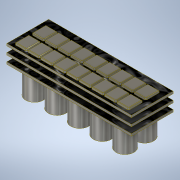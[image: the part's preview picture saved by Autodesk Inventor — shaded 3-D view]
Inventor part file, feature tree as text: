
AUTODESK INVENTOR PART (.ipt)
format: ipt  version: 2020 (Build 240168000, 168)  size: 654,336 bytes
history: native  units: mm
features: chamfer x16, extrude x9, sketch x9, other x2
ambient origin geometry x8: Origin, YZ Plane, XZ Plane, XY Plane, X Axis, Y Axis, Z Axis, Center Point
bodies: Body1 (feature_tree)
feature tree (36):
  other  "Bryła1"
  extrude  "Wyciągnięcie proste1"  Depth=18.73mm
  extrude  "Wyciągnięcie proste2"  Depth=9.365mm
  chamfer  "Faza1"  Distance=55.88mm
  chamfer  "Faza2"  Distance=27.94mm
  chamfer  "Faza3"  Distance=1.0mm
  extrude  "Wyciągnięcie proste3"  Depth=6.03mm
  chamfer  "Faza4"  Distance=5.08mm
  extrude  "Wyciągnięcie proste4"  Depth=2.54mm
  chamfer  "Faza5"  Distance=1.27mm
  chamfer  "Faza6"  Distance=5.08mm
  chamfer  "Faza7"  Distance=6.03mm
  chamfer  "Faza8"  Distance=1.27mm
  chamfer  "Faza9"  Distance=0.64mm
  chamfer  "Faza10"  Distance=5.08mm
  chamfer  "Faza11"  Distance=0.64mm
  chamfer  "Faza12"  Distance=5.08mm
  chamfer  "Faza13"  Distance=0.64mm
  chamfer  "Faza14"  Distance=5.08mm
  chamfer  "Faza15"  Distance=0.64mm
  chamfer  "Faza16"  Distance=5.08mm
  other  "Płaszczyzna konstrukcyjna1"
  extrude  "Wyciągnięcie proste5"  Depth=5.08mm
  extrude  "Wyciągnięcie proste6"  Depth=5.08mm
  extrude  "Wyciągnięcie proste7"  Depth=5.08mm
  extrude  "Wyciągnięcie proste8"  Depth=0.64mm
  extrude  "Wyciągnięcie proste9"  Depth=0.64mm
  sketch  "Szkic1"
  sketch  "Szkic2"
  sketch  "Szkic3"
  sketch  "Szkic4"
  sketch  "Szkic5"
  sketch  "Szkic6"
  sketch  "Szkic7"
  sketch  "Szkic8"
  sketch  "Szkic9"
